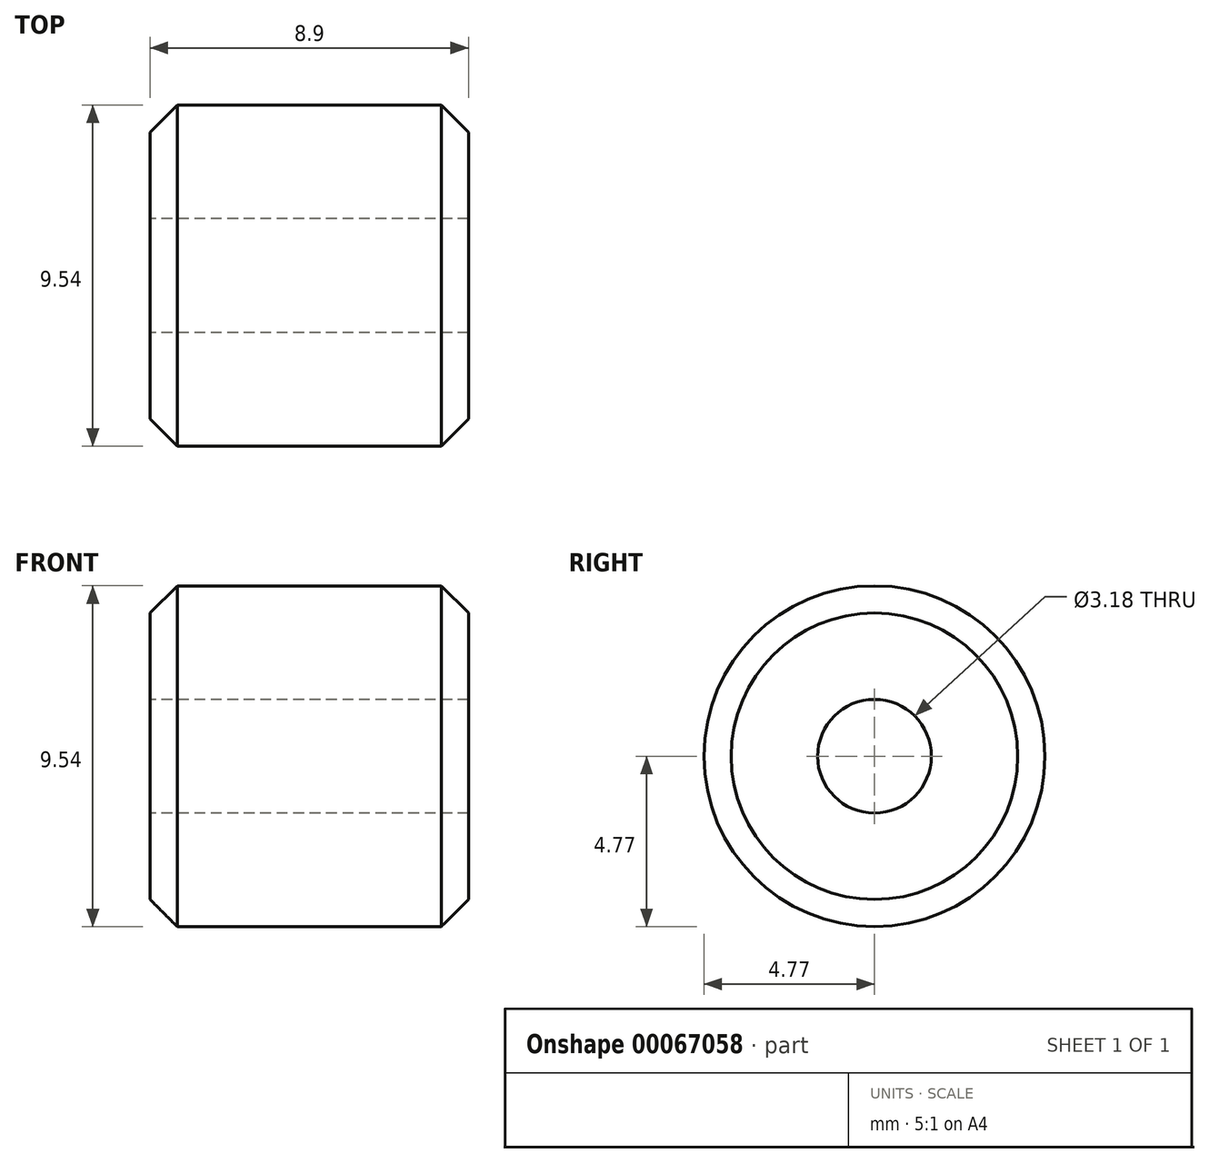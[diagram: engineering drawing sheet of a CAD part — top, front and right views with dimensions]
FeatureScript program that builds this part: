
annotation { "Feature Type Name" : "Feature", "Feature Type Description" : "" }
export const myFeature = defineFeature(function(context is Context, id is Id, definition is map)
    precondition{}
    {
        {
            var Q0;
            Q0=qCreatedBy(makeId("Right.planeOp"),FACE);
            var sketch = newSketch(context, id + "F0", { "sketchPlane" : qUnion([Q0])});
            skCircle(sketch, "E0", {"center": v(0, 0) * mm, "radius": 4.77 * mm});
            skCircle(sketch, "E1", {"center": v(0, 0) * mm, "radius": 1.6 * mm});
            skSolve(sketch);
        }
        {
            var Q0;
            Q0=qSketchRegion(id+"F0",true);
            extrude(context, id + "F1", {"entities" : qUnion([Q0]), "endBound" : BoundingType.SYMMETRIC, "depth" : 8.9 * mm});
        }
        {
            var Q0;
            Q0=makeQuery(id+"F1.opExtrude","SWEPT_FACE",FACE,{"disambiguationData":[OSD([sQuery(id+"F0.wireOp",EDGE,"E0")])]});
            chamfer(context, id + "F2", {"entities" : qUnion([Q0]), "width" : 0.76 * mm, "tangentPropagation" : true});
        }
    });
